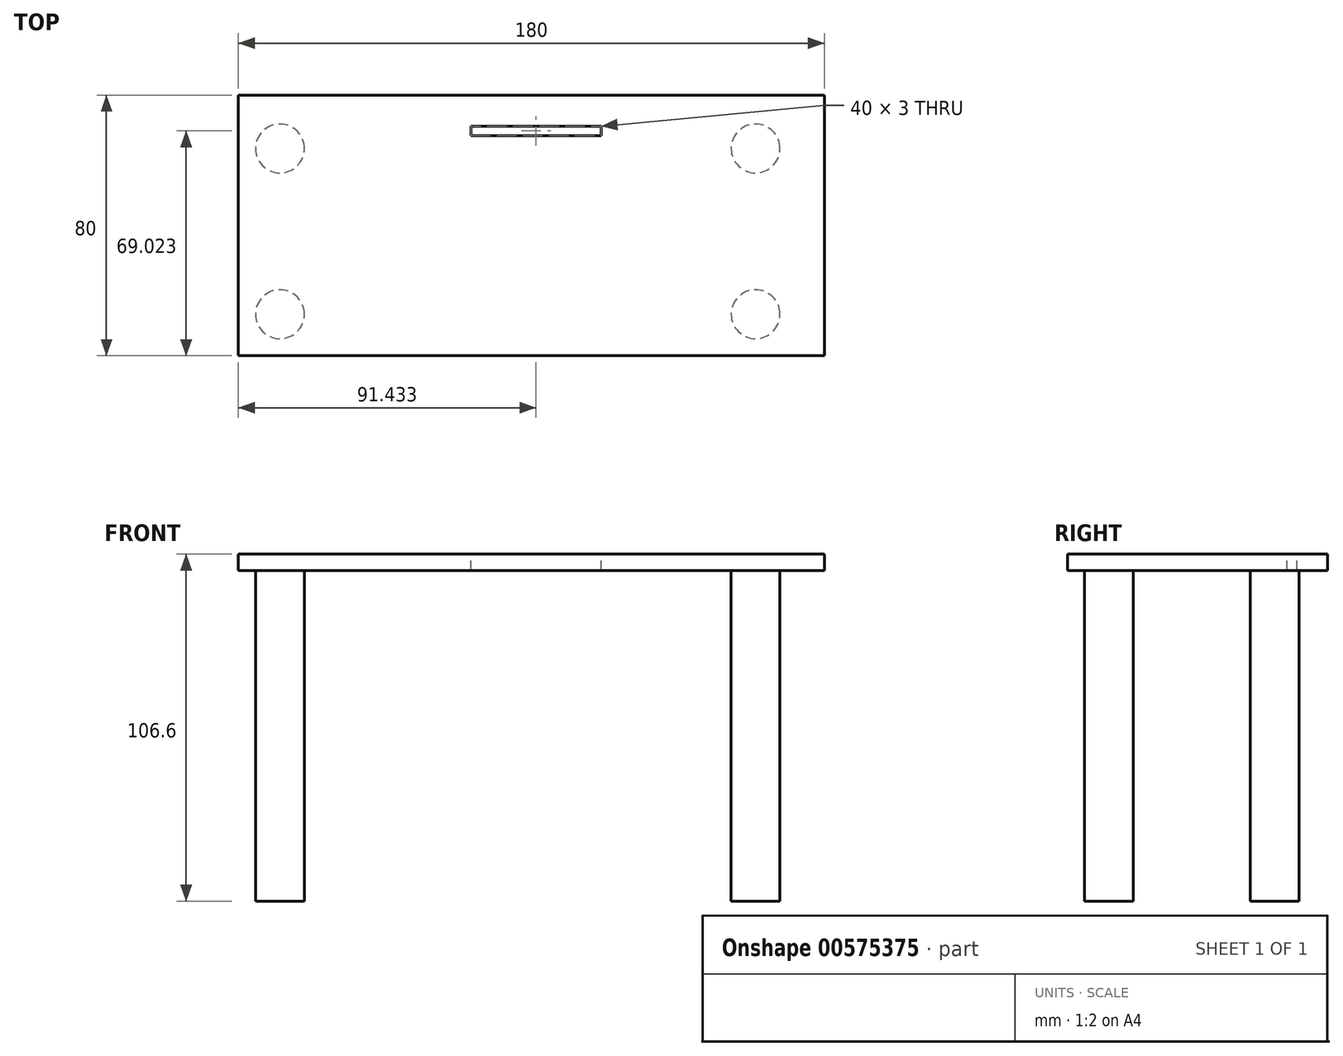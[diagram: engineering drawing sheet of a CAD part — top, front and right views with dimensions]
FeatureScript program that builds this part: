
annotation { "Feature Type Name" : "Feature", "Feature Type Description" : "" }
export const myFeature = defineFeature(function(context is Context, id is Id, definition is map)
    precondition{}
    {
        {
            var Q0;
            Q0=qCreatedBy(makeId("Top.planeOp"),FACE);
            var sketch = newSketch(context, id + "F0", { "sketchPlane" : qUnion([Q0])});
            skLineSegment(sketch, "E0.bottom", {"start": v(-74.6, -80) * mm, "end": v(105.4, -80) * mm});
            skLineSegment(sketch, "E0.top", {"start": v(-74.6, 0) * mm, "end": v(105.4, 0) * mm});
            skLineSegment(sketch, "E0.left", {"start": v(-74.6, -80) * mm, "end": v(-74.6, 0) * mm});
            skLineSegment(sketch, "E0.right", {"start": v(105.4, -80) * mm, "end": v(105.4, 0) * mm});
            skCircle(sketch, "E1", {"center": v(-61.8, -67.3) * mm, "radius": 7.5 * mm});
            skCircle(sketch, "E2", {"center": v(-61.8, -16.37) * mm, "radius": 7.5 * mm});
            skCircle(sketch, "E3", {"center": v(84.29, -67.3) * mm, "radius": 7.5 * mm});
            skCircle(sketch, "E4", {"center": v(84.29, -16.37) * mm, "radius": 7.5 * mm});
            skLineSegment(sketch, "E5", {"start": v(-61.8, -67.3) * mm, "end": v(-61.8, -16.37) * mm});
            skLineSegment(sketch, "E6", {"start": v(-61.8, -16.37) * mm, "end": v(84.29, -16.37) * mm});
            skLineSegment(sketch, "E7", {"start": v(84.29, -67.3) * mm, "end": v(84.29, -16.37) * mm});
            skLineSegment(sketch, "E8", {"start": v(-61.8, -67.3) * mm, "end": v(84.29, -67.3) * mm});
            skSolve(sketch);
        }
        {
            var Q0;
            {var subQ0=sQuery(id+"F0.wireOp",EDGE,"E5");var subQ1=sQuery(id+"F0.wireOp",EDGE,"E1");var subQ2=makeQuery(id+"F0.imprint","INTERSECT",VERTEX,{"derivedFrom":[subQ1,subQ0]});Q0=makeQuery(id+"F0.imprint","IMPRINT",FACE,{"disambiguationData":[TD([[makeQuery(id+"F0.imprint","IMPRINT",EDGE,{"disambiguationData":[TD([[subQ2,-1.0]])],"derivedFrom":subQ1}),1.0]])]});}
            var Q1;
            {var subQ0=sQuery(id+"F0.wireOp",EDGE,"E7");var subQ1=sQuery(id+"F0.wireOp",EDGE,"E3");var subQ2=makeQuery(id+"F0.imprint","INTERSECT",VERTEX,{"derivedFrom":[subQ1,subQ0]});Q1=makeQuery(id+"F0.imprint","IMPRINT",FACE,{"disambiguationData":[TD([[makeQuery(id+"F0.imprint","IMPRINT",EDGE,{"disambiguationData":[TD([[subQ2,1.0]])],"derivedFrom":subQ1}),1.0]])]});}
            var Q2;
            {var subQ0=sQuery(id+"F0.wireOp",EDGE,"E6");var subQ1=sQuery(id+"F0.wireOp",EDGE,"E4");var subQ2=makeQuery(id+"F0.imprint","INTERSECT",VERTEX,{"derivedFrom":[subQ1,subQ0]});Q2=makeQuery(id+"F0.imprint","IMPRINT",FACE,{"disambiguationData":[TD([[makeQuery(id+"F0.imprint","IMPRINT",EDGE,{"disambiguationData":[TD([[subQ2,1.0]])],"derivedFrom":subQ1}),1.0]])]});}
            var Q3;
            {var subQ0=sQuery(id+"F0.wireOp",EDGE,"E5");var subQ1=sQuery(id+"F0.wireOp",EDGE,"E2");var subQ2=makeQuery(id+"F0.imprint","INTERSECT",VERTEX,{"derivedFrom":[subQ1,subQ0]});Q3=makeQuery(id+"F0.imprint","IMPRINT",FACE,{"disambiguationData":[TD([[makeQuery(id+"F0.imprint","IMPRINT",EDGE,{"disambiguationData":[TD([[subQ2,1.0]])],"derivedFrom":subQ1}),1.0]])]});}
            var Q4;
            {var subQ0=sQuery(id+"F0.wireOp",EDGE,"E5");var subQ1=sQuery(id+"F0.wireOp",EDGE,"E1");var subQ2=makeQuery(id+"F0.imprint","INTERSECT",VERTEX,{"derivedFrom":[subQ1,subQ0]});Q4=makeQuery(id+"F0.imprint","IMPRINT",FACE,{"disambiguationData":[TD([[makeQuery(id+"F0.imprint","IMPRINT",EDGE,{"disambiguationData":[TD([[subQ2,1.0]])],"derivedFrom":subQ1}),1.0]])]});}
            var Q5;
            {var subQ0=sQuery(id+"F0.wireOp",EDGE,"E7");var subQ1=sQuery(id+"F0.wireOp",EDGE,"E3");var subQ2=makeQuery(id+"F0.imprint","INTERSECT",VERTEX,{"derivedFrom":[subQ1,subQ0]});Q5=makeQuery(id+"F0.imprint","IMPRINT",FACE,{"disambiguationData":[TD([[makeQuery(id+"F0.imprint","IMPRINT",EDGE,{"disambiguationData":[TD([[subQ2,-1.0]])],"derivedFrom":subQ1}),1.0]])]});}
            var Q6;
            {var subQ0=sQuery(id+"F0.wireOp",EDGE,"E6");var subQ1=sQuery(id+"F0.wireOp",EDGE,"E4");var subQ2=makeQuery(id+"F0.imprint","INTERSECT",VERTEX,{"derivedFrom":[subQ1,subQ0]});Q6=makeQuery(id+"F0.imprint","IMPRINT",FACE,{"disambiguationData":[TD([[makeQuery(id+"F0.imprint","IMPRINT",EDGE,{"disambiguationData":[TD([[subQ2,-1.0]])],"derivedFrom":subQ1}),1.0]])]});}
            var Q7;
            {var subQ0=sQuery(id+"F0.wireOp",EDGE,"E5");var subQ1=sQuery(id+"F0.wireOp",EDGE,"E2");var subQ2=makeQuery(id+"F0.imprint","INTERSECT",VERTEX,{"derivedFrom":[subQ1,subQ0]});Q7=makeQuery(id+"F0.imprint","IMPRINT",FACE,{"disambiguationData":[TD([[makeQuery(id+"F0.imprint","IMPRINT",EDGE,{"disambiguationData":[TD([[subQ2,-1.0]])],"derivedFrom":subQ1}),1.0]])]});}
            extrude(context, id + "F1", {"entities" : qUnion([Q0, Q1, Q2, Q3, Q4, Q5, Q6, Q7]), "depth" : -101.6 * mm, "offsetDistance" : 25.4 * mm});
        }
        {
            var Q0;
            Q0=makeQuery(id+"F0.imprint","IMPRINT",FACE,{"disambiguationData":[TD([[makeQuery(id+"F0.imprint","IMPRINT",EDGE,{"derivedFrom":sQuery(id+"F0.wireOp",EDGE,"E0.bottom")}),1.0]])]});
            var Q1;
            {var subQ0=sQuery(id+"F0.wireOp",EDGE,"E5");var subQ1=sQuery(id+"F0.wireOp",EDGE,"E2");var subQ2=makeQuery(id+"F0.imprint","INTERSECT",VERTEX,{"derivedFrom":[subQ1,subQ0]});Q1=makeQuery(id+"F0.imprint","IMPRINT",FACE,{"disambiguationData":[TD([[makeQuery(id+"F0.imprint","IMPRINT",EDGE,{"disambiguationData":[TD([[subQ2,1.0]])],"derivedFrom":subQ1}),1.0]])]});}
            var Q2;
            {var subQ0=sQuery(id+"F0.wireOp",EDGE,"E6");var subQ1=sQuery(id+"F0.wireOp",EDGE,"E4");var subQ2=makeQuery(id+"F0.imprint","INTERSECT",VERTEX,{"derivedFrom":[subQ1,subQ0]});Q2=makeQuery(id+"F0.imprint","IMPRINT",FACE,{"disambiguationData":[TD([[makeQuery(id+"F0.imprint","IMPRINT",EDGE,{"disambiguationData":[TD([[subQ2,-1.0]])],"derivedFrom":subQ1}),1.0]])]});}
            var Q3;
            {var subQ0=sQuery(id+"F0.wireOp",EDGE,"E7");var subQ1=sQuery(id+"F0.wireOp",EDGE,"E3");var subQ2=makeQuery(id+"F0.imprint","INTERSECT",VERTEX,{"derivedFrom":[subQ1,subQ0]});Q3=makeQuery(id+"F0.imprint","IMPRINT",FACE,{"disambiguationData":[TD([[makeQuery(id+"F0.imprint","IMPRINT",EDGE,{"disambiguationData":[TD([[subQ2,1.0]])],"derivedFrom":subQ1}),1.0]])]});}
            var Q4;
            {var subQ0=sQuery(id+"F0.wireOp",EDGE,"E5");var subQ1=sQuery(id+"F0.wireOp",EDGE,"E1");var subQ2=makeQuery(id+"F0.imprint","INTERSECT",VERTEX,{"derivedFrom":[subQ1,subQ0]});Q4=makeQuery(id+"F0.imprint","IMPRINT",FACE,{"disambiguationData":[TD([[makeQuery(id+"F0.imprint","IMPRINT",EDGE,{"disambiguationData":[TD([[subQ2,1.0]])],"derivedFrom":subQ1}),1.0]])]});}
            var Q5;
            {var subQ0=sQuery(id+"F0.wireOp",EDGE,"E6");var subQ1=sQuery(id+"F0.wireOp",EDGE,"E4");var subQ2=makeQuery(id+"F0.imprint","INTERSECT",VERTEX,{"derivedFrom":[subQ1,subQ0]});Q5=makeQuery(id+"F0.imprint","IMPRINT",FACE,{"disambiguationData":[TD([[makeQuery(id+"F0.imprint","IMPRINT",EDGE,{"disambiguationData":[TD([[subQ2,1.0]])],"derivedFrom":subQ1}),1.0]])]});}
            var Q6;
            {var subQ0=sQuery(id+"F0.wireOp",EDGE,"E5");var subQ1=sQuery(id+"F0.wireOp",EDGE,"E1");var subQ2=makeQuery(id+"F0.imprint","INTERSECT",VERTEX,{"derivedFrom":[subQ1,subQ0]});Q6=makeQuery(id+"F0.imprint","IMPRINT",FACE,{"disambiguationData":[TD([[makeQuery(id+"F0.imprint","IMPRINT",EDGE,{"disambiguationData":[TD([[subQ2,-1.0]])],"derivedFrom":subQ1}),1.0]])]});}
            var Q7;
            {var subQ0=sQuery(id+"F0.wireOp",EDGE,"E5");var subQ1=sQuery(id+"F0.wireOp",EDGE,"E2");var subQ2=makeQuery(id+"F0.imprint","INTERSECT",VERTEX,{"derivedFrom":[subQ1,subQ0]});Q7=makeQuery(id+"F0.imprint","IMPRINT",FACE,{"disambiguationData":[TD([[makeQuery(id+"F0.imprint","IMPRINT",EDGE,{"disambiguationData":[TD([[subQ2,-1.0]])],"derivedFrom":subQ1}),1.0]])]});}
            var Q8;
            {var subQ0=sQuery(id+"F0.wireOp",EDGE,"E7");var subQ1=sQuery(id+"F0.wireOp",EDGE,"E3");var subQ2=makeQuery(id+"F0.imprint","INTERSECT",VERTEX,{"derivedFrom":[subQ1,subQ0]});Q8=makeQuery(id+"F0.imprint","IMPRINT",FACE,{"disambiguationData":[TD([[makeQuery(id+"F0.imprint","IMPRINT",EDGE,{"disambiguationData":[TD([[subQ2,-1.0]])],"derivedFrom":subQ1}),1.0]])]});}
            var Q9;
            {var subQ9=sQuery(id+"F0.wireOp",EDGE,"E5");var subQ13=sQuery(id+"F0.wireOp",EDGE,"E1");var subQ14=makeQuery(id+"F0.imprint","INTERSECT",VERTEX,{"derivedFrom":[subQ13,subQ9]});Q9=makeQuery(id+"F0.imprint","IMPRINT",FACE,{"disambiguationData":[TD([[makeQuery(id+"F0.imprint","IMPRINT",EDGE,{"disambiguationData":[TD([[subQ14,1.0]])],"derivedFrom":subQ13}),-1.0]])]});}
            extrude(context, id + "F2", {"entities" : qUnion([Q0, Q1, Q2, Q3, Q4, Q5, Q6, Q7, Q8, Q9]), "depth" : 5 * mm, "offsetDistance" : 25.4 * mm});
        }
        {
            var Q0;
            Q0=makeQuery(id+"F2.opExtrude","CAP_FACE",FACE,{"disambiguationData":[OSD([sQuery(id+"F0.wireOp",EDGE,"E0.bottom"),sQuery(id+"F0.wireOp",EDGE,"E0.top"),sQuery(id+"F0.wireOp",EDGE,"E0.left"),sQuery(id+"F0.wireOp",EDGE,"E0.right")])],"isStart":false});
            var sketch = newSketch(context, id + "F3", { "sketchPlane" : qUnion([Q0])});
            skLineSegment(sketch, "E9.bottom", {"start": v(-3.17, -9.48) * mm, "end": v(36.83, -9.48) * mm});
            skLineSegment(sketch, "E9.top", {"start": v(-3.17, -12.48) * mm, "end": v(36.83, -12.48) * mm});
            skLineSegment(sketch, "E9.left", {"start": v(-3.17, -9.48) * mm, "end": v(-3.17, -12.48) * mm});
            skLineSegment(sketch, "E9.right", {"start": v(36.83, -9.48) * mm, "end": v(36.83, -12.48) * mm});
            skSolve(sketch);
        }
        {
            var Q0;
            Q0=makeQuery(id+"F3.imprint","IMPRINT",FACE,{"disambiguationData":[TD([[makeQuery(id+"F3.imprint","IMPRINT",EDGE,{"derivedFrom":sQuery(id+"F3.wireOp",EDGE,"E9.bottom")}),-1.0]])]});
            extrude(context, id + "F4", {"entities" : qUnion([Q0]), "operationType" : NewBodyOperationType.REMOVE, "oppositeDirection" : true, "depth" : 25.4 * mm, "offsetDistance" : 25.4 * mm});
        }
    });
